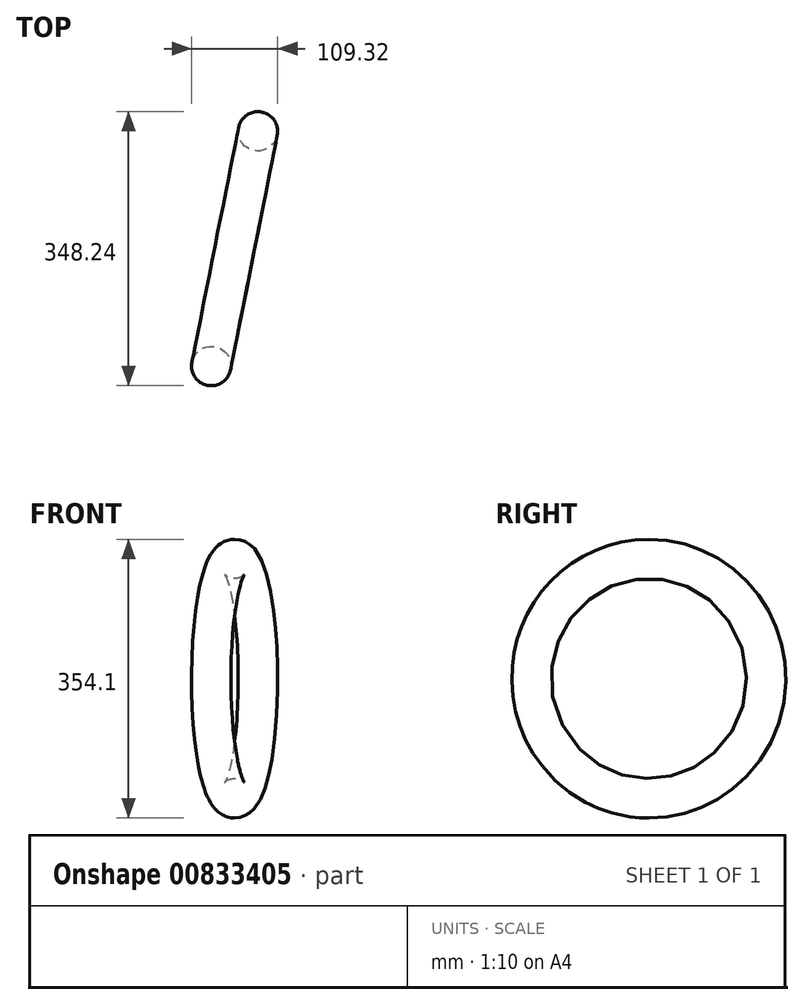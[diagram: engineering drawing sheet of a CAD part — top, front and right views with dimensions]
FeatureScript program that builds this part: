
annotation { "Feature Type Name" : "Feature", "Feature Type Description" : "" }
export const myFeature = defineFeature(function(context is Context, id is Id, definition is map)
    precondition{}
    {
        {
            var Q0;
            Q0=qCreatedBy(makeId("Front.planeOp"),FACE);
            var sketch = newSketch(context, id + "F0", { "sketchPlane" : qUnion([Q0])});
            skCircle(sketch, "E0", {"center": v(0, 0) * mm, "radius": 152 * mm});
            skLineSegment(sketch, "E1", {"start": v(0, 0) * mm, "end": v(0, -152) * mm});
            skLineSegment(sketch, "E2", {"start": v(0, -152) * mm, "end": v(139.9, -152) * mm});
            skSolve(sketch);
        }
        {
            var Q0;
            Q0=sQuery(id+"F0.wireOp",VERTEX,"E1.end");
            var Q1;
            Q1=sQuery(id+"F0.wireOp",EDGE,"E2");
            cPlane(context, id + "F1", {"entities" : qUnion([Q0, Q1]), "cplaneType" : CPlaneType.LINE_POINT, "offset" : 25.4 * mm, "width" : 152.4 * mm, "height" : 152.4 * mm});
        }
        {
            var Q0;
            Q0=qCreatedBy(id+"F1.planeOp",FACE);
            var sketch = newSketch(context, id + "F2", { "sketchPlane" : qUnion([Q0])});
            skCircle(sketch, "E3", {"center": v(0, -152.05) * mm, "radius": 25 * mm});
            skSolve(sketch);
        }
        {
            var Q0;
            Q0=makeQuery(id+"F2.imprint","IMPRINT",FACE,{"disambiguationData":[TD([[makeQuery(id+"F2.imprint","IMPRINT",EDGE,{"derivedFrom":sQuery(id+"F2.wireOp",EDGE,"E3")}),1.0]])]});
            var Q1;
            Q1=sQuery(id+"F0.wireOp",EDGE,"E0");
            sweep(context, id + "F3", {"profiles" : qUnion([Q0]), "path" : qUnion([Q1])});
        }
        {
            var Q0;
            Q0=makeQuery(id+"F3.opSweep","SWEPT_BODY",BODY,{"disambiguationData":[OSD([sQuery(id+"F0.wireOp",EDGE,"E0"),sQuery(id+"F2.wireOp",EDGE,"E3")])]});
            var Q1;
            Q1=makeQuery(id+"F3.opSweep","SWEPT_FACE",FACE,{"disambiguationData":[OSD([sQuery(id+"F0.wireOp",EDGE,"E0"),sQuery(id+"F2.wireOp",EDGE,"E3")])]});
            transform(context, id + "F4", {"entities" : qUnion([Q0]), "transformType" : TransformType.ROTATION, "transformAxis" : qUnion([Q1]), "angle" : 45 * degree, "makeCopy" : false});
        }
        {
            var Q0;
            Q0=makeQuery(id+"F3.opSweep","SWEPT_BODY",BODY,{"disambiguationData":[OSD([sQuery(id+"F0.wireOp",EDGE,"E0"),sQuery(id+"F2.wireOp",EDGE,"E3")])]});
            var Q1;
            Q1=sQuery(id+"F0.wireOp",EDGE,"E1");
            transform(context, id + "F5", {"entities" : qUnion([Q0]), "transformType" : TransformType.ROTATION, "transformAxis" : qUnion([Q1]), "angle" : 101.25 * degree, "makeCopy" : false});
        }
    });
